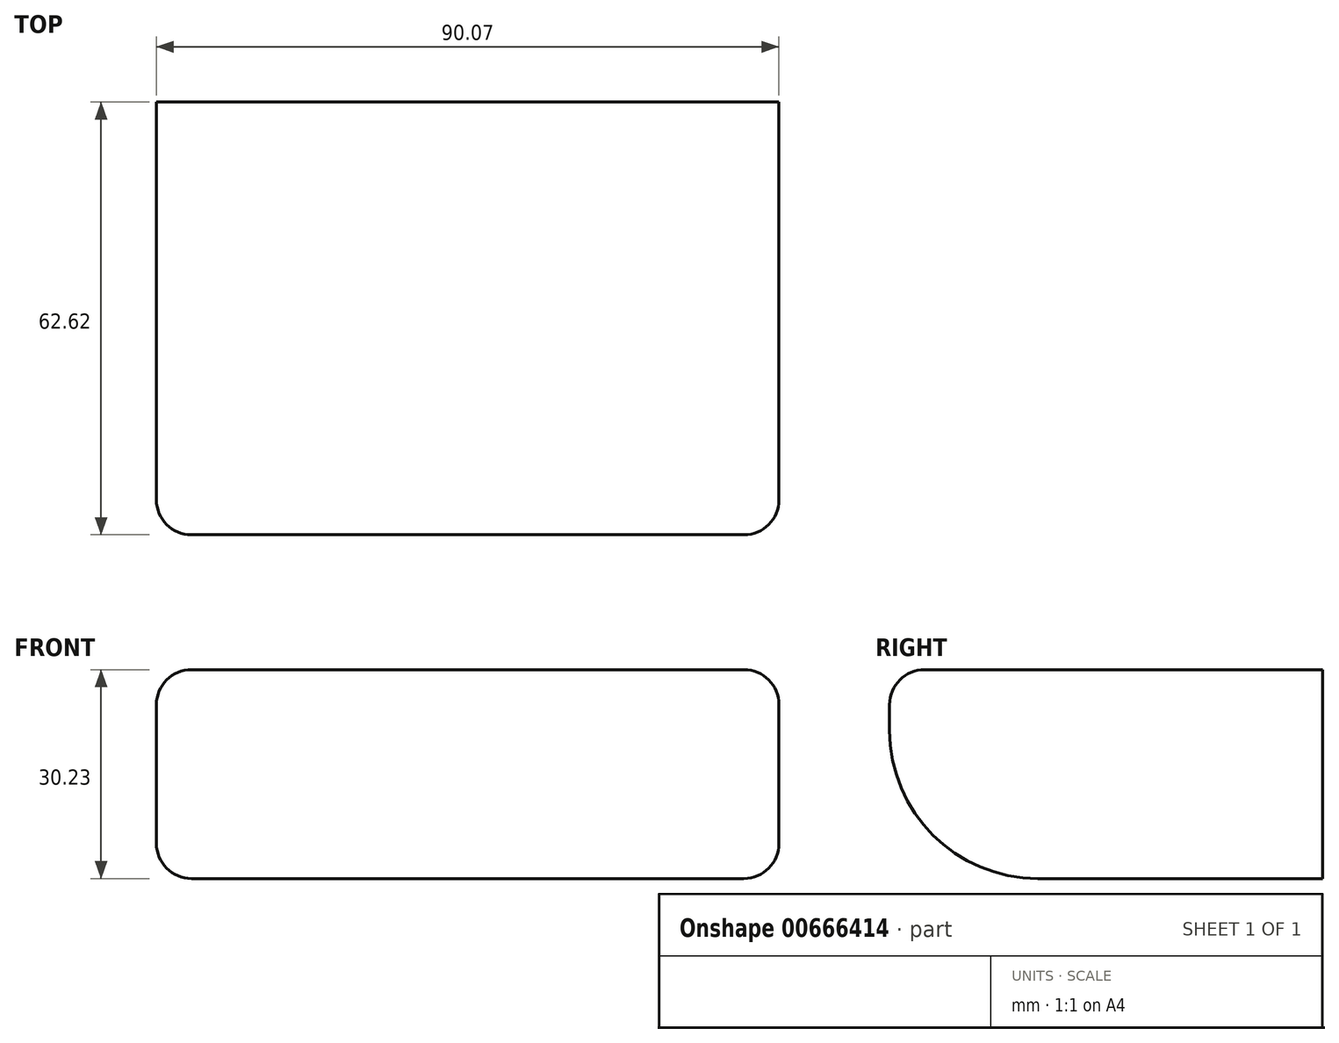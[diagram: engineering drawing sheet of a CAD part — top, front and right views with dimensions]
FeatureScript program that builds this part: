
annotation { "Feature Type Name" : "Feature", "Feature Type Description" : "" }
export const myFeature = defineFeature(function(context is Context, id is Id, definition is map)
    precondition{}
    {
        {
            var Q0;
            Q0=qCreatedBy(makeId("Top.planeOp"),FACE);
            var sketch = newSketch(context, id + "F0", { "sketchPlane" : qUnion([Q0])});
            skLineSegment(sketch, "E0.bottom", {"start": v(-47.67, 9.44) * mm, "end": v(42.4, 9.44) * mm});
            skLineSegment(sketch, "E0.top", {"start": v(-47.67, -53.18) * mm, "end": v(42.4, -53.18) * mm});
            skLineSegment(sketch, "E0.left", {"start": v(-47.67, 9.44) * mm, "end": v(-47.67, -53.18) * mm});
            skLineSegment(sketch, "E0.right", {"start": v(42.4, 9.44) * mm, "end": v(42.4, -53.18) * mm});
            skSolve(sketch);
        }
        {
            var Q0;
            Q0 = qSketchRegion(id + "F0", true);
            extrude(context, id + "F1", {"entities" : qUnion([Q0]), "depth" : 30.23 * mm, "offsetDistance" : 25.4 * mm});
        }
        {
            var Q0;
            Q0=makeQuery(id+"F1.opExtrude","CAP_EDGE",EDGE,{"disambiguationData":[OSD([sQuery(id+"F0.wireOp",EDGE,"E0.top")])],"isStart":true});
            fillet(context, id + "F2", {"entities" : qUnion([Q0]), "radius" : 21.46 * mm, "tangentPropagation" : true, "allowEdgeOverflow" : false});
        }
        {
            var Q0;
            Q0=makeQuery(id+"F1.opExtrude","CAP_EDGE",EDGE,{"disambiguationData":[OSD([sQuery(id+"F0.wireOp",EDGE,"E0.right")])],"isStart":true});
            var Q1;
            Q1=makeQuery(id+"F1.opExtrude","CAP_EDGE",EDGE,{"disambiguationData":[OSD([sQuery(id+"F0.wireOp",EDGE,"E0.left")])],"isStart":true});
            fillet(context, id + "F3", {"entities" : qUnion([Q0, Q1]), "radius" : 5.08 * mm, "tangentPropagation" : true, "allowEdgeOverflow" : false});
        }
        {
            var Q0;
            {var subQ0=sQuery(id+"F0.wireOp",EDGE,"E0.top");Q0=makeQuery(id+"F2.opFillet","BLEND_EDGE",EDGE,{"blendedFrom":[makeQuery(id+"F1.opExtrude","CAP_EDGE",EDGE,{"disambiguationData":[OSD([subQ0])],"isStart":true}),makeQuery(id+"F1.opExtrude","SWEPT_FACE",FACE,{"disambiguationData":[OSD([subQ0])]})],"blendedInto":[makeQuery(id+"F1.opExtrude","SWEPT_FACE",FACE,{"disambiguationData":[OSD([subQ0])]})]});}
            var Q1;
            Q1=makeQuery(id+"F1.opExtrude","SWEPT_FACE",FACE,{"disambiguationData":[OSD([sQuery(id+"F0.wireOp",EDGE,"E0.top")])]});
            var Q2;
            Q2=makeQuery(id+"F2.opFillet","BLEND_FACE",FACE,{"disambiguationData":[OSD([sQuery(id+"F0.wireOp",EDGE,"E0.top")])]});
            fillet(context, id + "F4", {"entities" : qUnion([Q0, Q1, Q2]), "radius" : 5.08 * mm, "tangentPropagation" : true, "allowEdgeOverflow" : false});
        }
    });
